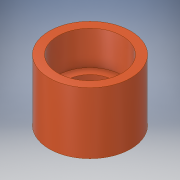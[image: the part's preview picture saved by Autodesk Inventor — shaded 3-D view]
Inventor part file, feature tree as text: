
AUTODESK INVENTOR PART (.ipt)
format: ipt  version: 2017 (Build 210142000, 142)  size: 151,552 bytes
history: native  units: in
note: dims shown in document units (in); Inventor stores cm internally (conversion verified against a paired STEP export)
features: revolve x1, sketch x1
ambient origin geometry x8: Origin, YZ Plane, XZ Plane, XY Plane, X Axis, Y Axis, Z Axis, Center Point
bodies: Body1 (feature_tree)
feature tree (2):
  revolve  "Revolution2"  [1 undecoded]
  sketch  "Sketch1"  dims[d0=0.25in d1=0.1718in d2=15.0deg d4=0.25in d5=1.5in d6=1.25in d7=0.25in d11=0.25in d13=0.5in d15=0.25in d16=0.25in d18=0.125in d19=0.5in d20=0.125in d21=0.25in d22=0.125in d23=0.125in d24=0.25in d25=0.5in d26=2.292in d27=0.5in d29=0.5in d30=90.0deg]
note: 1 required parameter value undecoded (feature->parameter linkage not recoverable at this tier; creation-order binding heuristic only, values carry confidence <= 0.55)
